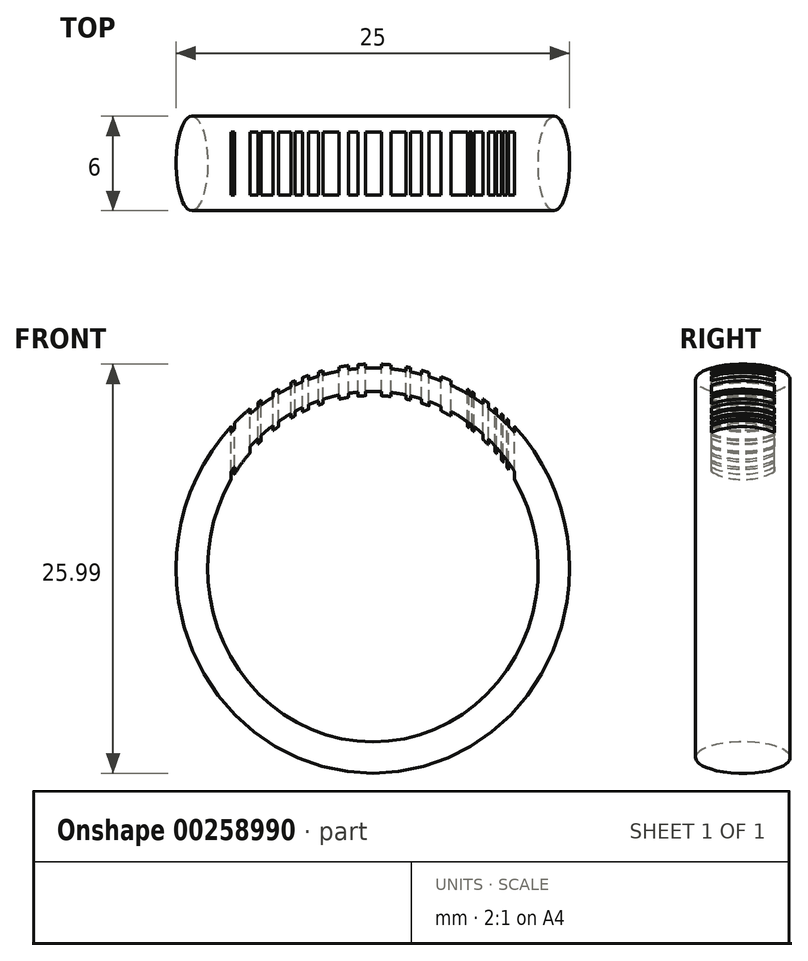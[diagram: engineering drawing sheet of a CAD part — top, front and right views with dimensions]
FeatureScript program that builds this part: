
annotation { "Feature Type Name" : "Feature", "Feature Type Description" : "" }
export const myFeature = defineFeature(function(context is Context, id is Id, definition is map)
    precondition{}
    {
        {
            var Q0;
            Q0=qCreatedBy(makeId("Front.planeOp"),FACE);
            var sketch = newSketch(context, id + "F0", { "sketchPlane" : qUnion([Q0])});
            skEllipse(sketch, "E0", {"center": v(0, 0) * mm, "majorRadius": 9.5 * mm, "minorRadius": 10 * mm, "majorAxis": v(1, 0)});
            skSolve(sketch);
        }
        {
            var Q0;
            Q0=qCreatedBy(makeId("Right.planeOp"),FACE);
            var sketch = newSketch(context, id + "F1", { "sketchPlane" : qUnion([Q0])});
            skEllipse(sketch, "E1", {"center": v(0, 12) * mm, "majorRadius": 3 * mm, "minorRadius": 1 * mm, "majorAxis": v(-1, 0)});
            skSolve(sketch);
        }
        {
            var Q0;
            Q0=makeQuery(id+"F1.imprint","IMPRINT",FACE,{"disambiguationData":[TD([[makeQuery(id+"F1.imprint","IMPRINT",EDGE,{"derivedFrom":sQuery(id+"F1.wireOp",EDGE,"E1")}),1.0]])]});
            var Q1;
            Q1=sQuery(id+"F0.wireOp",EDGE,"E0");
            sweep(context, id + "F2", {"profiles" : qUnion([Q0]), "path" : qUnion([Q1])});
        }
        {
            var Q0;
            Q0=qCreatedBy(makeId("Top.planeOp"),FACE);
            cPlane(context, id + "F3", {"entities" : qUnion([Q0]), "cplaneType" : CPlaneType.OFFSET, "offset" : 13 * mm, "width" : 150 * mm, "height" : 150 * mm});
        }
        {
            var Q0;
            Q0=qCreatedBy(id+"F3.planeOp",FACE);
            var sketch = newSketch(context, id + "F4", { "sketchPlane" : qUnion([Q0])});
            skLineSegment(sketch, "E2.bottom", {"start": v(-9, 2) * mm, "end": v(-8.8, 2) * mm});
            skLineSegment(sketch, "E2.top", {"start": v(-9, -2) * mm, "end": v(-8.8, -2) * mm});
            skLineSegment(sketch, "E2.left", {"start": v(-9, 2) * mm, "end": v(-9, -2) * mm});
            skLineSegment(sketch, "E2.right", {"start": v(9, 2) * mm, "end": v(9, -2) * mm});
            skLineSegment(sketch, "E3", {"start": v(-8.8, 2) * mm, "end": v(-8.8, -2) * mm});
            skLineSegment(sketch, "E4", {"start": v(-7.3, -2) * mm, "end": v(-7.3, 2) * mm});
            skLineSegment(sketch, "E5", {"start": v(-7.8, -2) * mm, "end": v(-7.8, 2) * mm});
            skLineSegment(sketch, "E6", {"start": v(-7.1, -2) * mm, "end": v(-7.1, 2) * mm});
            skLineSegment(sketch, "E7", {"start": v(-2.16, -2) * mm, "end": v(-2.16, 2) * mm});
            skLineSegment(sketch, "E8", {"start": v(-6, -2) * mm, "end": v(-6, 2) * mm});
            skLineSegment(sketch, "E9", {"start": v(-3.46, -2) * mm, "end": v(-3.46, 2) * mm});
            skLineSegment(sketch, "E10", {"start": v(0.54, -2) * mm, "end": v(0.54, 2) * mm});
            skLineSegment(sketch, "E11", {"start": v(-1.56, -2) * mm, "end": v(-1.56, 2) * mm});
            skLineSegment(sketch, "E12", {"start": v(-5.2, -2) * mm, "end": v(-5.2, 2) * mm});
            skLineSegment(sketch, "E13", {"start": v(-3.16, -2) * mm, "end": v(-3.16, 2) * mm});
            skLineSegment(sketch, "E14", {"start": v(1.14, -2) * mm, "end": v(1.14, 2) * mm});
            skLineSegment(sketch, "E15", {"start": v(-0.96, -2) * mm, "end": v(-0.96, 2) * mm});
            skLineSegment(sketch, "E16", {"start": v(-4.95, -2) * mm, "end": v(-4.95, 2) * mm});
            skLineSegment(sketch, "E17", {"start": v(-6.35, -2) * mm, "end": v(-6.35, 2) * mm});
            skLineSegment(sketch, "E18.left", {"start": v(-4.48, -2) * mm, "end": v(-4.48, 2) * mm});
            skLineSegment(sketch, "E18.right", {"start": v(-4.08, -2) * mm, "end": v(-4.08, 2) * mm});
            skLineSegment(sketch, "E19", {"start": v(-0.46, -2) * mm, "end": v(-0.46, 2) * mm});
            skLineSegment(sketch, "E20.left", {"start": v(2.1, -2) * mm, "end": v(2.1, 2) * mm});
            skLineSegment(sketch, "E20.right", {"start": v(2.4, -2) * mm, "end": v(2.4, 2) * mm});
            skLineSegment(sketch, "E21.left", {"start": v(3.1, -2) * mm, "end": v(3.1, 2) * mm});
            skLineSegment(sketch, "E21.right", {"start": v(3.58, -2) * mm, "end": v(3.58, 2) * mm});
            skLineSegment(sketch, "E22.left", {"start": v(4.33, -2) * mm, "end": v(4.33, 2) * mm});
            skLineSegment(sketch, "E22.right", {"start": v(4.95, -2) * mm, "end": v(4.95, 2) * mm});
            skLineSegment(sketch, "E23.left", {"start": v(6.12, -2) * mm, "end": v(6.12, 2) * mm});
            skLineSegment(sketch, "E23.right", {"start": v(6.01, -2) * mm, "end": v(6.01, 2) * mm});
            skLineSegment(sketch, "E24.left", {"start": v(6.3, 2) * mm, "end": v(6.3, -2) * mm});
            skLineSegment(sketch, "E24.right", {"start": v(6.4, 2) * mm, "end": v(6.4, -2) * mm});
            skLineSegment(sketch, "E25.left", {"start": v(7, -2) * mm, "end": v(7, 2) * mm});
            skLineSegment(sketch, "E25.right", {"start": v(7.33, -2) * mm, "end": v(7.33, 2) * mm});
            skLineSegment(sketch, "E26.left", {"start": v(7.74, -2) * mm, "end": v(7.74, 2) * mm});
            skLineSegment(sketch, "E26.right", {"start": v(7.86, -2) * mm, "end": v(7.86, 2) * mm});
            skLineSegment(sketch, "E27.left", {"start": v(8.16, -2) * mm, "end": v(8.16, 2) * mm});
            skLineSegment(sketch, "E27.right", {"start": v(8.28, -2) * mm, "end": v(8.28, 2) * mm});
            skLineSegment(sketch, "E28.left", {"start": v(8.52, -2) * mm, "end": v(8.52, 2) * mm});
            skLineSegment(sketch, "E28.right", {"start": v(8.62, -2) * mm, "end": v(8.62, 2) * mm});
            skLineSegment(sketch, "E29.trimOffspring", {"start": v(-7.8, 2) * mm, "end": v(-7.3, 2) * mm});
            skLineSegment(sketch, "E30.trimOffspring", {"start": v(-7.8, -2) * mm, "end": v(-7.3, -2) * mm});
            skLineSegment(sketch, "E31.trimOffspring", {"start": v(-7.1, -2) * mm, "end": v(-6.35, -2) * mm});
            skLineSegment(sketch, "E32.trimOffspring", {"start": v(-7.1, 2) * mm, "end": v(-6.35, 2) * mm});
            skLineSegment(sketch, "E33.trimOffspring", {"start": v(-6, 2) * mm, "end": v(-5.2, 2) * mm});
            skLineSegment(sketch, "E34.trimOffspring", {"start": v(-6, -2) * mm, "end": v(-5.2, -2) * mm});
            skLineSegment(sketch, "E35.trimOffspring", {"start": v(-4.95, -2) * mm, "end": v(-4.48, -2) * mm});
            skLineSegment(sketch, "E36.trimOffspring", {"start": v(-4.95, 2) * mm, "end": v(-3.46, 2) * mm});
            skLineSegment(sketch, "E37.trimOffspring", {"start": v(-4.08, -2) * mm, "end": v(-3.46, -2) * mm});
            skLineSegment(sketch, "E38.trimOffspring", {"start": v(-3.16, -2) * mm, "end": v(-2.16, -2) * mm});
            skLineSegment(sketch, "E39.trimOffspring", {"start": v(-3.16, 2) * mm, "end": v(-2.16, 2) * mm});
            skLineSegment(sketch, "E40.trimOffspring", {"start": v(-1.56, -2) * mm, "end": v(-0.96, -2) * mm});
            skLineSegment(sketch, "E41.trimOffspring", {"start": v(-1.56, 2) * mm, "end": v(-0.96, 2) * mm});
            skLineSegment(sketch, "E42.trimOffspring", {"start": v(-0.46, 2) * mm, "end": v(0.54, 2) * mm});
            skLineSegment(sketch, "E43.trimOffspring", {"start": v(-0.46, -2) * mm, "end": v(0.54, -2) * mm});
            skLineSegment(sketch, "E44.trimOffspring", {"start": v(1.14, -2) * mm, "end": v(2.1, -2) * mm});
            skLineSegment(sketch, "E45.trimOffspring", {"start": v(1.14, 2) * mm, "end": v(2.1, 2) * mm});
            skLineSegment(sketch, "E46.trimOffspring", {"start": v(2.4, -2) * mm, "end": v(3.1, -2) * mm});
            skLineSegment(sketch, "E47.trimOffspring", {"start": v(2.4, 2) * mm, "end": v(3.1, 2) * mm});
            skLineSegment(sketch, "E48.trimOffspring", {"start": v(3.58, -2) * mm, "end": v(4.33, -2) * mm});
            skLineSegment(sketch, "E49.trimOffspring", {"start": v(3.58, 2) * mm, "end": v(4.33, 2) * mm});
            skLineSegment(sketch, "E50.trimOffspring", {"start": v(4.95, -2) * mm, "end": v(6.01, -2) * mm});
            skLineSegment(sketch, "E51.trimOffspring", {"start": v(4.95, 2) * mm, "end": v(6.01, 2) * mm});
            skLineSegment(sketch, "E52.trimOffspring", {"start": v(6.12, 2) * mm, "end": v(6.3, 2) * mm});
            skLineSegment(sketch, "E53.trimOffspring", {"start": v(6.4, 2) * mm, "end": v(7, 2) * mm});
            skLineSegment(sketch, "E54.trimOffspring", {"start": v(6.4, -2) * mm, "end": v(7, -2) * mm});
            skLineSegment(sketch, "E55.trimOffspring", {"start": v(6.12, -2) * mm, "end": v(6.3, -2) * mm});
            skLineSegment(sketch, "E56.trimOffspring", {"start": v(7.33, -2) * mm, "end": v(7.74, -2) * mm});
            skLineSegment(sketch, "E57.trimOffspring", {"start": v(7.33, 2) * mm, "end": v(7.74, 2) * mm});
            skLineSegment(sketch, "E58.trimOffspring", {"start": v(7.86, 2) * mm, "end": v(8.16, 2) * mm});
            skLineSegment(sketch, "E59.trimOffspring", {"start": v(8.28, 2) * mm, "end": v(8.52, 2) * mm});
            skLineSegment(sketch, "E60.trimOffspring", {"start": v(8.62, 2) * mm, "end": v(9, 2) * mm});
            skLineSegment(sketch, "E61.trimOffspring", {"start": v(8.62, -2) * mm, "end": v(9, -2) * mm});
            skLineSegment(sketch, "E62.trimOffspring", {"start": v(8.28, -2) * mm, "end": v(8.52, -2) * mm});
            skLineSegment(sketch, "E63.trimOffspring", {"start": v(7.86, -2) * mm, "end": v(8.16, -2) * mm});
            skSolve(sketch);
        }
        {
            var Q0;
            Q0=makeQuery(id+"F4.imprint","IMPRINT",FACE,{"disambiguationData":[TD([[makeQuery(id+"F4.imprint","IMPRINT",EDGE,{"derivedFrom":sQuery(id+"F4.wireOp",EDGE,"E2.bottom")}),-1.0]])]});
            var Q1;
            Q1=makeQuery(id+"F4.imprint","IMPRINT",FACE,{"disambiguationData":[TD([[makeQuery(id+"F4.imprint","IMPRINT",EDGE,{"derivedFrom":sQuery(id+"F4.wireOp",EDGE,"E4")}),1.0]])]});
            var Q2;
            Q2=makeQuery(id+"F4.imprint","IMPRINT",FACE,{"disambiguationData":[TD([[makeQuery(id+"F4.imprint","IMPRINT",EDGE,{"derivedFrom":sQuery(id+"F4.wireOp",EDGE,"E6")}),-1.0]])]});
            var Q3;
            Q3=makeQuery(id+"F4.imprint","IMPRINT",FACE,{"disambiguationData":[TD([[makeQuery(id+"F4.imprint","IMPRINT",EDGE,{"derivedFrom":sQuery(id+"F4.wireOp",EDGE,"E8")}),-1.0]])]});
            var Q4;
            {var subQ0=sQuery(id+"F4.wireOp",EDGE,"E16");Q4=makeQuery(id+"F4.imprint","IMPRINT",FACE,{"disambiguationData":[TD([[makeQuery(id+"F4.imprint","IMPRINT",EDGE,{"derivedFrom":subQ0}),-1.0]])]});}
            var Q5;
            {var subQ0=sQuery(id+"F4.wireOp",EDGE,"E9");Q5=makeQuery(id+"F4.imprint","IMPRINT",FACE,{"disambiguationData":[TD([[makeQuery(id+"F4.imprint","IMPRINT",EDGE,{"derivedFrom":subQ0}),1.0]])]});}
            var Q6;
            Q6=makeQuery(id+"F4.imprint","IMPRINT",FACE,{"disambiguationData":[TD([[makeQuery(id+"F4.imprint","IMPRINT",EDGE,{"derivedFrom":sQuery(id+"F4.wireOp",EDGE,"E7")}),1.0]])]});
            var Q7;
            Q7=makeQuery(id+"F4.imprint","IMPRINT",FACE,{"disambiguationData":[TD([[makeQuery(id+"F4.imprint","IMPRINT",EDGE,{"derivedFrom":sQuery(id+"F4.wireOp",EDGE,"E11")}),-1.0]])]});
            var Q8;
            Q8=makeQuery(id+"F4.imprint","IMPRINT",FACE,{"disambiguationData":[TD([[makeQuery(id+"F4.imprint","IMPRINT",EDGE,{"derivedFrom":sQuery(id+"F4.wireOp",EDGE,"E10")}),1.0]])]});
            var Q9;
            Q9=makeQuery(id+"F4.imprint","IMPRINT",FACE,{"disambiguationData":[TD([[makeQuery(id+"F4.imprint","IMPRINT",EDGE,{"derivedFrom":sQuery(id+"F4.wireOp",EDGE,"E14")}),-1.0]])]});
            var Q10;
            Q10=makeQuery(id+"F4.imprint","IMPRINT",FACE,{"disambiguationData":[TD([[makeQuery(id+"F4.imprint","IMPRINT",EDGE,{"derivedFrom":sQuery(id+"F4.wireOp",EDGE,"E20.right")}),-1.0]])]});
            var Q11;
            Q11=makeQuery(id+"F4.imprint","IMPRINT",FACE,{"disambiguationData":[TD([[makeQuery(id+"F4.imprint","IMPRINT",EDGE,{"derivedFrom":sQuery(id+"F4.wireOp",EDGE,"E21.right")}),-1.0]])]});
            var Q12;
            Q12=makeQuery(id+"F4.imprint","IMPRINT",FACE,{"disambiguationData":[TD([[makeQuery(id+"F4.imprint","IMPRINT",EDGE,{"derivedFrom":sQuery(id+"F4.wireOp",EDGE,"E22.right")}),-1.0]])]});
            var Q13;
            Q13=makeQuery(id+"F4.imprint","IMPRINT",FACE,{"disambiguationData":[TD([[makeQuery(id+"F4.imprint","IMPRINT",EDGE,{"derivedFrom":sQuery(id+"F4.wireOp",EDGE,"E23.left")}),-1.0]])]});
            var Q14;
            Q14=makeQuery(id+"F4.imprint","IMPRINT",FACE,{"disambiguationData":[TD([[makeQuery(id+"F4.imprint","IMPRINT",EDGE,{"derivedFrom":sQuery(id+"F4.wireOp",EDGE,"E24.right")}),1.0]])]});
            var Q15;
            Q15=makeQuery(id+"F4.imprint","IMPRINT",FACE,{"disambiguationData":[TD([[makeQuery(id+"F4.imprint","IMPRINT",EDGE,{"derivedFrom":sQuery(id+"F4.wireOp",EDGE,"E25.right")}),-1.0]])]});
            var Q16;
            Q16=makeQuery(id+"F4.imprint","IMPRINT",FACE,{"disambiguationData":[TD([[makeQuery(id+"F4.imprint","IMPRINT",EDGE,{"derivedFrom":sQuery(id+"F4.wireOp",EDGE,"E26.right")}),-1.0]])]});
            var Q17;
            Q17=makeQuery(id+"F4.imprint","IMPRINT",FACE,{"disambiguationData":[TD([[makeQuery(id+"F4.imprint","IMPRINT",EDGE,{"derivedFrom":sQuery(id+"F4.wireOp",EDGE,"E27.right")}),-1.0]])]});
            var Q18;
            Q18=makeQuery(id+"F4.imprint","IMPRINT",FACE,{"disambiguationData":[TD([[makeQuery(id+"F4.imprint","IMPRINT",EDGE,{"derivedFrom":sQuery(id+"F4.wireOp",EDGE,"E2.right")}),-1.0]])]});
            extrude(context, id + "F5", {"entities" : qUnion([Q0, Q1, Q2, Q3, Q4, Q5, Q6, Q7, Q8, Q9, Q10, Q11, Q12, Q13, Q14, Q15, Q16, Q17, Q18]), "operationType" : NewBodyOperationType.REMOVE, "oppositeDirection" : true, "depth" : 10 * mm});
        }
    });
